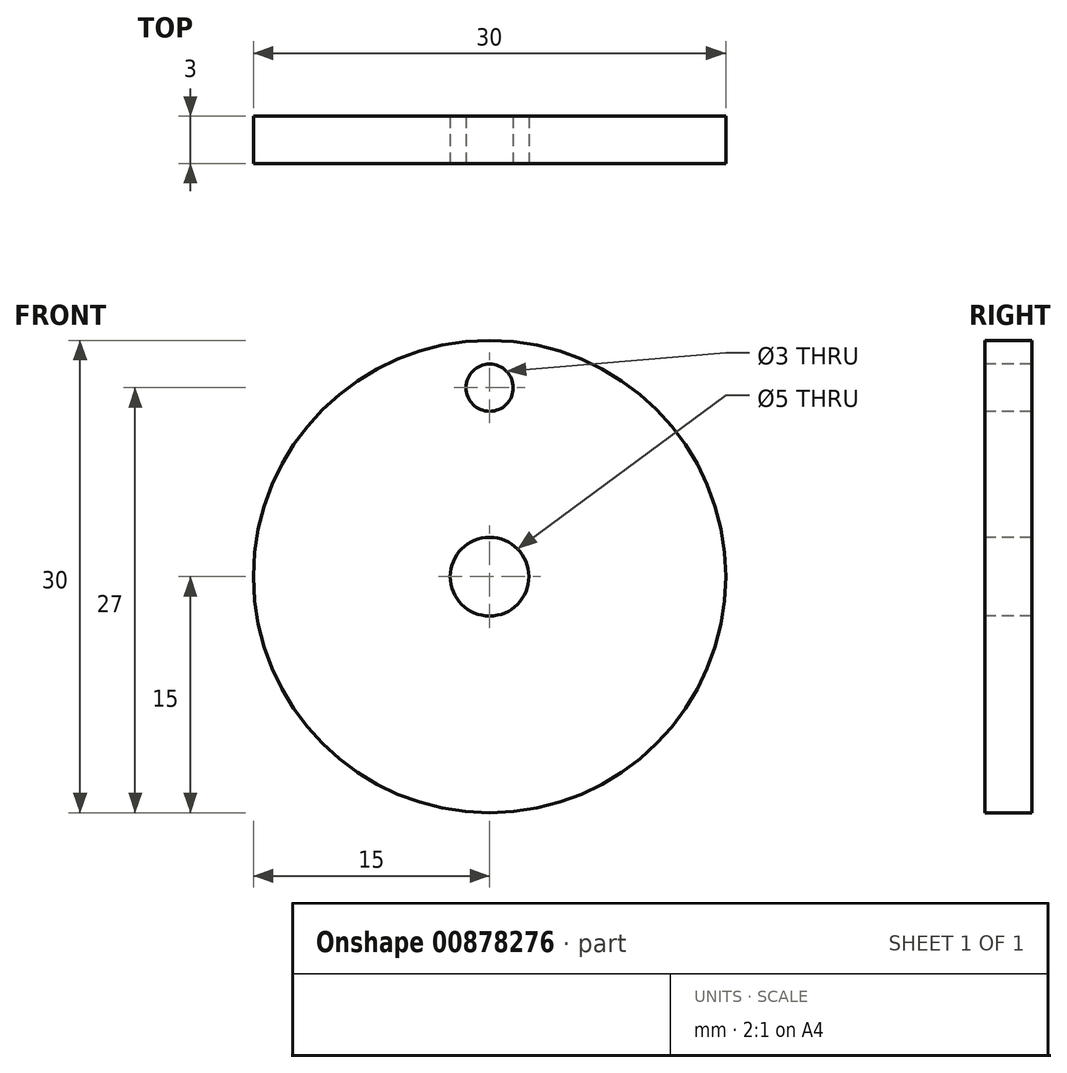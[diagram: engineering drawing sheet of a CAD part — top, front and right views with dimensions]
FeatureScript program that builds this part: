
annotation { "Feature Type Name" : "Feature", "Feature Type Description" : "" }
export const myFeature = defineFeature(function(context is Context, id is Id, definition is map)
    precondition{}
    {
        {
            var Q0;
            Q0=qCreatedBy(makeId("Front.planeOp"),FACE);
            var sketch = newSketch(context, id + "F0", { "sketchPlane" : qUnion([Q0])});
            skCircle(sketch, "E0", {"center": v(0, 0) * mm, "radius": 15 * mm});
            skSolve(sketch);
        }
        {
            var Q0;
            Q0 = qSketchRegion(id + "F0", true);
            extrude(context, id + "F1", {"entities" : qUnion([Q0]), "depth" : 3 * mm, "offsetDistance" : 25 * mm});
        }
        {
            var Q0;
            Q0=makeQuery(id+"F1.opExtrude","CAP_FACE",FACE,{"disambiguationData":[OSD([sQuery(id+"F0.wireOp",EDGE,"E0")])],"isStart":false});
            var sketch = newSketch(context, id + "F2", { "sketchPlane" : qUnion([Q0])});
            skCircle(sketch, "E1", {"center": v(0, 12) * mm, "radius": 1.5 * mm});
            skSolve(sketch);
        }
        {
            var Q0;
            Q0 = qSketchRegion(id + "F2", true);
            extrude(context, id + "F3", {"entities" : qUnion([Q0]), "operationType" : NewBodyOperationType.REMOVE, "endBound" : BoundingType.UP_TO_NEXT, "oppositeDirection" : true, "depth" : 25 * mm, "offsetDistance" : 25 * mm});
        }
        {
            var Q0;
            Q0=makeQuery(id+"F1.opExtrude","CAP_FACE",FACE,{"disambiguationData":[OSD([sQuery(id+"F0.wireOp",EDGE,"E0")])],"isStart":false});
            var sketch = newSketch(context, id + "F4", { "sketchPlane" : qUnion([Q0])});
            skCircle(sketch, "E2", {"center": v(0, 0) * mm, "radius": 2.5 * mm});
            skSolve(sketch);
        }
        {
            var Q0;
            Q0 = qSketchRegion(id + "F4", true);
            extrude(context, id + "F5", {"entities" : qUnion([Q0]), "operationType" : NewBodyOperationType.REMOVE, "endBound" : BoundingType.UP_TO_NEXT, "oppositeDirection" : true, "depth" : 25 * mm, "offsetDistance" : 25 * mm});
        }
    });
